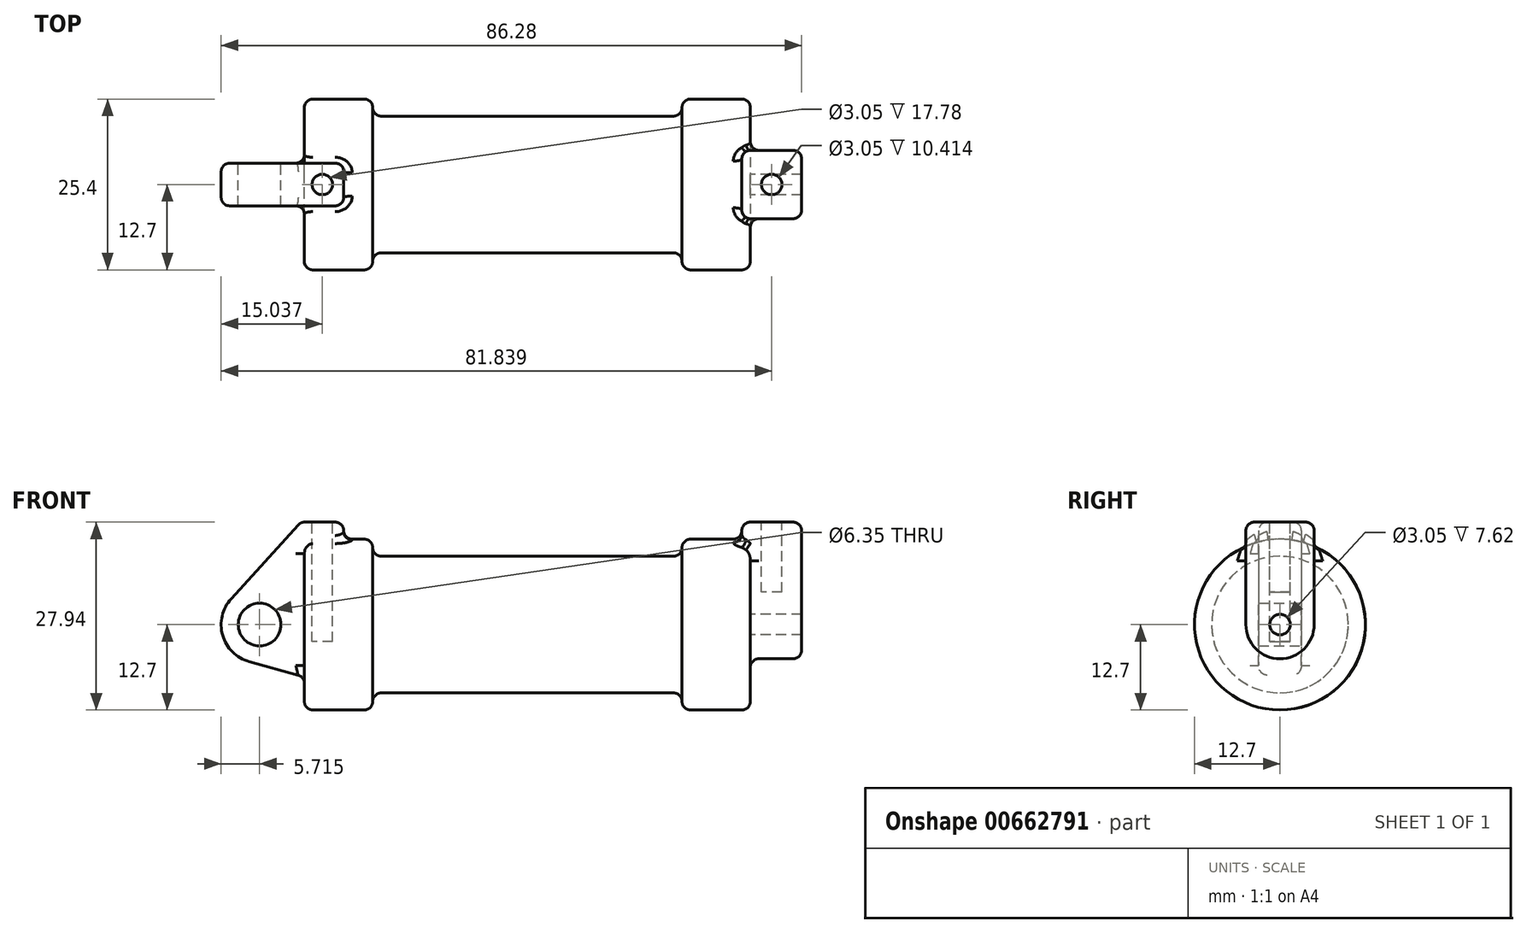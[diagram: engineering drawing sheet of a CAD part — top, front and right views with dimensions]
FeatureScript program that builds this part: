
annotation { "Feature Type Name" : "Feature", "Feature Type Description" : "" }
export const myFeature = defineFeature(function(context is Context, id is Id, definition is map)
    precondition{}
    {
        {
            var Q0;
            Q0=qCreatedBy(makeId("Front.planeOp"),FACE);
            var sketch = newSketch(context, id + "F0", { "sketchPlane" : qUnion([Q0])});
            skLineSegment(sketch, "E0", {"start": v(0, 0) * mm, "end": v(0, 12.7) * mm});
            skLineSegment(sketch, "E1", {"start": v(0, 12.7) * mm, "end": v(10.16, 12.7) * mm});
            skLineSegment(sketch, "E2", {"start": v(10.16, 12.7) * mm, "end": v(10.16, 10.16) * mm});
            skLineSegment(sketch, "E3", {"start": v(10.16, 10.16) * mm, "end": v(56.13, 10.16) * mm});
            skLineSegment(sketch, "E4", {"start": v(56.13, 10.16) * mm, "end": v(56.13, 12.7) * mm});
            skLineSegment(sketch, "E5", {"start": v(56.13, 12.7) * mm, "end": v(66.3, 12.7) * mm});
            skLineSegment(sketch, "E6", {"start": v(66.3, 12.7) * mm, "end": v(66.3, 0) * mm});
            skLineSegment(sketch, "E7", {"start": v(66.3, 0) * mm, "end": v(0, 0) * mm});
            skLineSegment(sketch, "E8", {"start": v(5.84, 15.24) * mm, "end": v(-0.5, 15.24) * mm});
            skLineSegment(sketch, "E9", {"start": v(-0.5, 15.24) * mm, "end": v(-10.88, 3.85) * mm});
            skLineSegment(sketch, "E10", {"start": v(0, 0) * mm, "end": v(-6.65, 0) * mm});
            skCircle(sketch, "E11", {"center": v(-6.65, 0) * mm, "radius": 5.72 * mm});
            skCircle(sketch, "E12", {"center": v(-6.65, 0) * mm, "radius": 3.18 * mm});
            skLineSegment(sketch, "E13", {"start": v(5.84, 15.24) * mm, "end": v(5.84, -9.4) * mm});
            skLineSegment(sketch, "E14", {"start": v(5.84, -9.4) * mm, "end": v(-8.18, -5.5) * mm});
            skSolve(sketch);
        }
        {
            var Q0;
            {var subQ0=sQuery(id+"F0.wireOp",EDGE,"E2");Q0=makeQuery(id+"F0.imprint","IMPRINT",FACE,{"disambiguationData":[TD([[makeQuery(id+"F0.imprint","IMPRINT",EDGE,{"derivedFrom":subQ0}),-1.0]])]});}
            var Q1;
            {var subQ0=sQuery(id+"F0.wireOp",EDGE,"E0");Q1=makeQuery(id+"F0.imprint","IMPRINT",FACE,{"disambiguationData":[TD([[makeQuery(id+"F0.imprint","IMPRINT",EDGE,{"derivedFrom":subQ0}),-1.0]])]});}
            var Q2;
            Q2=sQuery(id+"F0.wireOp",EDGE,"E7");
            revolve(context, id + "F1", {"entities" : qUnion([Q0, Q1]), "axis" : qUnion([Q2]), "revolveType" : RevolveType.FULL});
        }
        {
            var Q0;
            {var subQ1=sQuery(id+"F0.wireOp",EDGE,"E0");Q0=makeQuery(id+"F0.imprint","IMPRINT",FACE,{"disambiguationData":[TD([[makeQuery(id+"F0.imprint","IMPRINT",EDGE,{"derivedFrom":subQ1}),1.0]])]});}
            var Q1;
            {var subQ0=sQuery(id+"F0.wireOp",EDGE,"E0");Q1=makeQuery(id+"F0.imprint","IMPRINT",FACE,{"disambiguationData":[TD([[makeQuery(id+"F0.imprint","IMPRINT",EDGE,{"derivedFrom":subQ0}),-1.0]])]});}
            var Q2;
            {var subQ0=sQuery(id+"F0.wireOp",EDGE,"E14");Q2=makeQuery(id+"F0.imprint","IMPRINT",FACE,{"disambiguationData":[TD([[makeQuery(id+"F0.imprint","IMPRINT",EDGE,{"derivedFrom":subQ0}),-1.0]])]});}
            var Q3;
            {var subQ5=sQuery(id+"F0.wireOp",EDGE,"E12");Q3=makeQuery(id+"F0.imprint","IMPRINT",FACE,{"disambiguationData":[TD([[makeQuery(id+"F0.imprint","IMPRINT",EDGE,{"derivedFrom":subQ5}),-1.0]])]});}
            extrude(context, id + "F2", {"entities" : qUnion([Q0, Q1, Q2, Q3]), "operationType" : NewBodyOperationType.ADD, "endBound" : BoundingType.SYMMETRIC, "depth" : 6.35 * mm, "offsetDistance" : 25.4 * mm});
        }
        {
            var Q0;
            Q0=makeQuery(id+"F1.opRevolve","SWEPT_FACE",FACE,{"disambiguationData":[OSD([sQuery(id+"F0.wireOp",EDGE,"E6")])]});
            var sketch = newSketch(context, id + "F3", { "sketchPlane" : qUnion([Q0])});
            skCircle(sketch, "E15", {"center": v(0, 0) * mm, "radius": 1.52 * mm});
            skCircle(sketch, "E16", {"center": v(0, 0) * mm, "radius": 5.08 * mm});
            skLineSegment(sketch, "E17.bottom", {"start": v(-5.08, 15.24) * mm, "end": v(5.08, 15.24) * mm});
            skLineSegment(sketch, "E17.left", {"start": v(-5.08, 15.24) * mm, "end": v(-5.08, 0) * mm});
            skLineSegment(sketch, "E17.right", {"start": v(5.08, 15.24) * mm, "end": v(5.08, 0) * mm});
            skSolve(sketch);
        }
        {
            var Q0;
            Q0 = qSketchRegion(id + "F3", true);
            extrude(context, id + "F4", {"entities" : qUnion([Q0]), "operationType" : NewBodyOperationType.ADD, "depth" : 7.62 * mm, "offsetDistance" : 25.4 * mm, "hasSecondDirection" : true, "secondDirectionOppositeDirection" : true, "secondDirectionDepth" : 1.27 * mm});
        }
        {
            var Q0;
            Q0=makeQuery(id+"F4.opExtrude","SWEPT_FACE",FACE,{"disambiguationData":[OSD([sQuery(id+"F3.wireOp",EDGE,"E17.bottom")])]});
            var sketch = newSketch(context, id + "F5", { "sketchPlane" : qUnion([Q0])});
            skCircle(sketch, "E18", {"center": v(2.67, 0) * mm, "radius": 1.52 * mm});
            skCircle(sketch, "E19", {"center": v(69.47, 0) * mm, "radius": 1.52 * mm});
            skCircle(sketch, "E20", {"center": v(2.67, 0) * mm, "radius": 3.17 * mm, "construction": true});
            skLineSegment(sketch, "E21", {"start": v(73.91, 5.08) * mm, "end": v(65.02, -5.08) * mm, "construction": true});
            skLineSegment(sketch, "E22", {"start": v(65.02, 5.08) * mm, "end": v(73.91, -5.08) * mm, "construction": true});
            skSolve(sketch);
        }
        {
            var Q0;
            Q0=makeQuery(id+"F5.imprint","IMPRINT",FACE,{"disambiguationData":[TD([[makeQuery(id+"F5.imprint","IMPRINT",EDGE,{"derivedFrom":sQuery(id+"F5.wireOp",EDGE,"E18")}),1.0]])]});
            var Q1;
            Q1=sQuery(id+"F5.wireOp",EDGE,"E18");
            extrude(context, id + "F6", {"entities" : qUnion([Q0]), "operationType" : NewBodyOperationType.REMOVE, "surfaceEntities" : qUnion([Q1]), "oppositeDirection" : true, "depth" : 17.78 * mm, "offsetDistance" : 25.4 * mm});
        }
        {
            var Q0;
            Q0=makeQuery(id+"F4.opExtrude","SWEPT_FACE",FACE,{"disambiguationData":[OSD([sQuery(id+"F3.wireOp",EDGE,"E17.bottom")])]});
            var sketch = newSketch(context, id + "F7", { "sketchPlane" : qUnion([Q0])});
            skLineSegment(sketch, "E23.0", {"start": v(65.02, 5.08) * mm, "end": v(73.91, -5.08) * mm, "construction": true});
            skLineSegment(sketch, "E24.0", {"start": v(73.91, 5.08) * mm, "end": v(65.02, -5.08) * mm, "construction": true});
            skCircle(sketch, "E25.0", {"center": v(69.47, 0) * mm, "radius": 1.52 * mm});
            skSolve(sketch);
        }
        {
            var Q0;
            Q0=makeQuery(id+"F5.imprint","IMPRINT",FACE,{"disambiguationData":[TD([[makeQuery(id+"F5.imprint","IMPRINT",EDGE,{"derivedFrom":sQuery(id+"F5.wireOp",EDGE,"E19")}),1.0]])]});
            var Q1;
            Q1=sQuery(id+"F7.wireOp",EDGE,"E23.0");
            var Q2;
            Q2=sQuery(id+"F7.wireOp",EDGE,"E24.0");
            extrude(context, id + "F8", {"entities" : qUnion([Q0]), "operationType" : NewBodyOperationType.REMOVE, "surfaceEntities" : qUnion([Q1, Q2]), "oppositeDirection" : true, "depth" : 10.4 * mm, "offsetDistance" : 25.4 * mm});
        }
        {
            var Q0;
            Q0=makeQuery(id+"F1.opRevolve","SWEPT_EDGE",EDGE,{"disambiguationData":[OSD([sQuery(id+"F0.wireOp",EDGE,"E2"),sQuery(id+"F0.wireOp",EDGE,"E3")])]});
            var Q1;
            Q1=makeQuery(id+"F1.opRevolve","SWEPT_EDGE",EDGE,{"disambiguationData":[OSD([sQuery(id+"F0.wireOp",EDGE,"E1"),sQuery(id+"F0.wireOp",EDGE,"E2")])]});
            var Q2;
            Q2=makeQuery(id+"F1.opRevolve","SWEPT_EDGE",EDGE,{"disambiguationData":[OSD([sQuery(id+"F0.wireOp",EDGE,"E3"),sQuery(id+"F0.wireOp",EDGE,"E4")])]});
            var Q3;
            Q3=makeQuery(id+"F1.opRevolve","SWEPT_EDGE",EDGE,{"disambiguationData":[OSD([sQuery(id+"F0.wireOp",EDGE,"E4"),sQuery(id+"F0.wireOp",EDGE,"E5")])]});
            var Q4;
            Q4=makeQuery(id+"F1.opRevolve","SWEPT_EDGE",EDGE,{"disambiguationData":[OSD([sQuery(id+"F0.wireOp",EDGE,"E0"),sQuery(id+"F0.wireOp",EDGE,"E1")])]});
            var Q5;
            Q5=makeQuery(id+"F1.opRevolve","SWEPT_EDGE",EDGE,{"disambiguationData":[OSD([sQuery(id+"F0.wireOp",EDGE,"E5"),sQuery(id+"F0.wireOp",EDGE,"E6")])]});
            fillet(context, id + "F9", {"entities" : qUnion([Q0, Q1, Q2, Q3, Q4, Q5]), "radius" : 1.27 * mm, "tangentPropagation" : true, "allowEdgeOverflow" : false});
        }
        {
            var Q0;
            Q0=makeQuery(id+"F2.boolean.opBoolean","INTERSECT",EDGE,{"derivedFrom":[makeQuery(id+"F1.opRevolve","SWEPT_FACE",FACE,{"disambiguationData":[OSD([sQuery(id+"F0.wireOp",EDGE,"E0")])]}),makeQuery(id+"F2.opExtrude","CAP_FACE",FACE,{"disambiguationData":[OSD([sQuery(id+"F0.wireOp",EDGE,"E8"),sQuery(id+"F0.wireOp",EDGE,"E9"),sQuery(id+"F0.wireOp",EDGE,"E11"),sQuery(id+"F0.wireOp",EDGE,"E12"),sQuery(id+"F0.wireOp",EDGE,"E13"),sQuery(id+"F0.wireOp",EDGE,"E14")])],"isStart":false})]});
            var Q1;
            Q1=makeQuery(id+"F2.boolean.opBoolean","INTERSECT",EDGE,{"derivedFrom":[makeQuery(id+"F1.opRevolve","SWEPT_FACE",FACE,{"disambiguationData":[OSD([sQuery(id+"F0.wireOp",EDGE,"E1")])]}),makeQuery(id+"F2.opExtrude","CAP_FACE",FACE,{"disambiguationData":[OSD([sQuery(id+"F0.wireOp",EDGE,"E8"),sQuery(id+"F0.wireOp",EDGE,"E9"),sQuery(id+"F0.wireOp",EDGE,"E11"),sQuery(id+"F0.wireOp",EDGE,"E12"),sQuery(id+"F0.wireOp",EDGE,"E13"),sQuery(id+"F0.wireOp",EDGE,"E14")])],"isStart":false})]});
            var Q2;
            Q2=makeQuery(id+"F9.opFillet","BLEND_EDGE",EDGE,{"blendedFrom":[makeQuery(id+"F1.opRevolve","SWEPT_EDGE",EDGE,{"disambiguationData":[OSD([sQuery(id+"F0.wireOp",EDGE,"E0"),sQuery(id+"F0.wireOp",EDGE,"E1")])]}),makeQuery(id+"F2.opExtrude","CAP_FACE",FACE,{"disambiguationData":[OSD([sQuery(id+"F0.wireOp",EDGE,"E8"),sQuery(id+"F0.wireOp",EDGE,"E9"),sQuery(id+"F0.wireOp",EDGE,"E11"),sQuery(id+"F0.wireOp",EDGE,"E12"),sQuery(id+"F0.wireOp",EDGE,"E13"),sQuery(id+"F0.wireOp",EDGE,"E14")])],"isStart":false})],"blendedInto":[makeQuery(id+"F2.opExtrude","CAP_FACE",FACE,{"disambiguationData":[OSD([sQuery(id+"F0.wireOp",EDGE,"E8"),sQuery(id+"F0.wireOp",EDGE,"E9"),sQuery(id+"F0.wireOp",EDGE,"E11"),sQuery(id+"F0.wireOp",EDGE,"E12"),sQuery(id+"F0.wireOp",EDGE,"E13"),sQuery(id+"F0.wireOp",EDGE,"E14")])],"isStart":false})]});
            var Q3;
            Q3=makeQuery(id+"F2.opExtrude","CAP_EDGE",EDGE,{"disambiguationData":[OSD([sQuery(id+"F0.wireOp",EDGE,"E13")])],"isStart":false});
            var Q4;
            Q4=makeQuery(id+"F2.opExtrude","CAP_EDGE",EDGE,{"disambiguationData":[OSD([sQuery(id+"F0.wireOp",EDGE,"E8")])],"isStart":false});
            var Q5;
            Q5=makeQuery(id+"F2.opExtrude","CAP_EDGE",EDGE,{"disambiguationData":[OSD([sQuery(id+"F0.wireOp",EDGE,"E9")])],"isStart":false});
            var Q6;
            Q6=makeQuery(id+"F2.opExtrude","CAP_EDGE",EDGE,{"disambiguationData":[OSD([sQuery(id+"F0.wireOp",EDGE,"E11")])],"isStart":false});
            var Q7;
            Q7=makeQuery(id+"F2.opExtrude","CAP_EDGE",EDGE,{"disambiguationData":[OSD([sQuery(id+"F0.wireOp",EDGE,"E14")])],"isStart":false});
            var Q8;
            Q8=makeQuery(id+"F2.opExtrude","CAP_EDGE",EDGE,{"disambiguationData":[OSD([sQuery(id+"F0.wireOp",EDGE,"E13")])],"isStart":true});
            var Q9;
            Q9=makeQuery(id+"F2.opExtrude","CAP_EDGE",EDGE,{"disambiguationData":[OSD([sQuery(id+"F0.wireOp",EDGE,"E8")])],"isStart":true});
            var Q10;
            Q10=makeQuery(id+"F2.opExtrude","CAP_EDGE",EDGE,{"disambiguationData":[OSD([sQuery(id+"F0.wireOp",EDGE,"E9")])],"isStart":true});
            var Q11;
            Q11=makeQuery(id+"F2.opExtrude","CAP_EDGE",EDGE,{"disambiguationData":[OSD([sQuery(id+"F0.wireOp",EDGE,"E11")])],"isStart":true});
            var Q12;
            Q12=makeQuery(id+"F2.opExtrude","CAP_EDGE",EDGE,{"disambiguationData":[OSD([sQuery(id+"F0.wireOp",EDGE,"E14")])],"isStart":true});
            var Q13;
            Q13=makeQuery(id+"F2.boolean.opBoolean","INTERSECT",EDGE,{"derivedFrom":[makeQuery(id+"F1.opRevolve","SWEPT_FACE",FACE,{"disambiguationData":[OSD([sQuery(id+"F0.wireOp",EDGE,"E0")])]}),makeQuery(id+"F2.opExtrude","CAP_FACE",FACE,{"disambiguationData":[OSD([sQuery(id+"F0.wireOp",EDGE,"E8"),sQuery(id+"F0.wireOp",EDGE,"E9"),sQuery(id+"F0.wireOp",EDGE,"E11"),sQuery(id+"F0.wireOp",EDGE,"E12"),sQuery(id+"F0.wireOp",EDGE,"E13"),sQuery(id+"F0.wireOp",EDGE,"E14")])],"isStart":true})]});
            var Q14;
            Q14=makeQuery(id+"F2.boolean.opBoolean","INTERSECT",EDGE,{"derivedFrom":[makeQuery(id+"F1.opRevolve","SWEPT_FACE",FACE,{"disambiguationData":[OSD([sQuery(id+"F0.wireOp",EDGE,"E1")])]}),makeQuery(id+"F2.opExtrude","CAP_FACE",FACE,{"disambiguationData":[OSD([sQuery(id+"F0.wireOp",EDGE,"E8"),sQuery(id+"F0.wireOp",EDGE,"E9"),sQuery(id+"F0.wireOp",EDGE,"E11"),sQuery(id+"F0.wireOp",EDGE,"E12"),sQuery(id+"F0.wireOp",EDGE,"E13"),sQuery(id+"F0.wireOp",EDGE,"E14")])],"isStart":true})]});
            var Q15;
            Q15=makeQuery(id+"F9.opFillet","BLEND_EDGE",EDGE,{"blendedFrom":[makeQuery(id+"F1.opRevolve","SWEPT_EDGE",EDGE,{"disambiguationData":[OSD([sQuery(id+"F0.wireOp",EDGE,"E0"),sQuery(id+"F0.wireOp",EDGE,"E1")])]}),makeQuery(id+"F2.opExtrude","CAP_FACE",FACE,{"disambiguationData":[OSD([sQuery(id+"F0.wireOp",EDGE,"E8"),sQuery(id+"F0.wireOp",EDGE,"E9"),sQuery(id+"F0.wireOp",EDGE,"E11"),sQuery(id+"F0.wireOp",EDGE,"E12"),sQuery(id+"F0.wireOp",EDGE,"E13"),sQuery(id+"F0.wireOp",EDGE,"E14")])],"isStart":true})],"blendedInto":[makeQuery(id+"F2.opExtrude","CAP_FACE",FACE,{"disambiguationData":[OSD([sQuery(id+"F0.wireOp",EDGE,"E8"),sQuery(id+"F0.wireOp",EDGE,"E9"),sQuery(id+"F0.wireOp",EDGE,"E11"),sQuery(id+"F0.wireOp",EDGE,"E12"),sQuery(id+"F0.wireOp",EDGE,"E13"),sQuery(id+"F0.wireOp",EDGE,"E14")])],"isStart":true})]});
            var Q16;
            Q16=makeQuery(id+"F2.opExtrude","SWEPT_EDGE",EDGE,{"disambiguationData":[OSD([sQuery(id+"F0.wireOp",EDGE,"E8"),sQuery(id+"F0.wireOp",EDGE,"E9")])]});
            var Q17;
            Q17=makeQuery(id+"F2.opExtrude","SWEPT_EDGE",EDGE,{"disambiguationData":[OSD([sQuery(id+"F0.wireOp",EDGE,"E8"),sQuery(id+"F0.wireOp",EDGE,"E13")])]});
            var Q18;
            Q18=makeQuery(id+"F2.boolean.opBoolean","INTERSECT",EDGE,{"derivedFrom":[makeQuery(id+"F1.opRevolve","SWEPT_FACE",FACE,{"disambiguationData":[OSD([sQuery(id+"F0.wireOp",EDGE,"E1")])]}),makeQuery(id+"F2.opExtrude","SWEPT_FACE",FACE,{"disambiguationData":[OSD([sQuery(id+"F0.wireOp",EDGE,"E13")])]})]});
            var Q19;
            Q19=makeQuery(id+"F2.boolean.opBoolean","INTERSECT",EDGE,{"derivedFrom":[makeQuery(id+"F1.opRevolve","SWEPT_FACE",FACE,{"disambiguationData":[OSD([sQuery(id+"F0.wireOp",EDGE,"E0")])]}),makeQuery(id+"F2.opExtrude","SWEPT_FACE",FACE,{"disambiguationData":[OSD([sQuery(id+"F0.wireOp",EDGE,"E14")])]})]});
            fillet(context, id + "F10", {"entities" : qUnion([Q0, Q1, Q2, Q3, Q4, Q5, Q6, Q7, Q8, Q9, Q10, Q11, Q12, Q13, Q14, Q15, Q16, Q17, Q18, Q19]), "radius" : 1.27 * mm, "tangentPropagation" : true, "allowEdgeOverflow" : false});
        }
        {
            var Q0;
            Q0=makeQuery(id+"F4.opExtrude","CAP_EDGE",EDGE,{"disambiguationData":[OSD([sQuery(id+"F3.wireOp",EDGE,"E17.bottom")])],"isStart":false});
            var Q1;
            Q1=makeQuery(id+"F4.opExtrude","SWEPT_EDGE",EDGE,{"disambiguationData":[OSD([sQuery(id+"F3.wireOp",EDGE,"E17.bottom"),sQuery(id+"F3.wireOp",EDGE,"E17.left")])]});
            var Q2;
            Q2=makeQuery(id+"F4.opExtrude","CAP_EDGE",EDGE,{"disambiguationData":[OSD([sQuery(id+"F3.wireOp",EDGE,"E17.bottom")])],"isStart":true});
            var Q3;
            Q3=makeQuery(id+"F4.opExtrude","SWEPT_EDGE",EDGE,{"disambiguationData":[OSD([sQuery(id+"F3.wireOp",EDGE,"E17.bottom"),sQuery(id+"F3.wireOp",EDGE,"E17.right")])]});
            var Q4;
            Q4=makeQuery(id+"F4.opExtrude","CAP_EDGE",EDGE,{"disambiguationData":[OSD([sQuery(id+"F3.wireOp",EDGE,"E17.right")])],"isStart":false});
            var Q5;
            Q5=makeQuery(id+"F4.opExtrude","CAP_EDGE",EDGE,{"disambiguationData":[OSD([sQuery(id+"F3.wireOp",EDGE,"E17.left")])],"isStart":false});
            var Q6;
            Q6=makeQuery(id+"F4.opExtrude","CAP_EDGE",EDGE,{"disambiguationData":[OSD([sQuery(id+"F3.wireOp",EDGE,"E16")])],"isStart":false});
            var Q7;
            Q7=makeQuery(id+"F4.boolean.opBoolean","INTERSECT",EDGE,{"derivedFrom":[makeQuery(id+"F1.opRevolve","SWEPT_FACE",FACE,{"disambiguationData":[OSD([sQuery(id+"F0.wireOp",EDGE,"E6")])]}),makeQuery(id+"F4.opExtrude","SWEPT_FACE",FACE,{"disambiguationData":[OSD([sQuery(id+"F3.wireOp",EDGE,"E17.left")])]})]});
            var Q8;
            Q8=makeQuery(id+"F4.opExtrude","CAP_EDGE",EDGE,{"disambiguationData":[OSD([sQuery(id+"F3.wireOp",EDGE,"E17.left")])],"isStart":true});
            var Q9;
            Q9=makeQuery(id+"F9.opFillet","BLEND_EDGE",EDGE,{"blendedFrom":[makeQuery(id+"F1.opRevolve","SWEPT_EDGE",EDGE,{"disambiguationData":[OSD([sQuery(id+"F0.wireOp",EDGE,"E5"),sQuery(id+"F0.wireOp",EDGE,"E6")])]}),makeQuery(id+"F4.opExtrude","SWEPT_FACE",FACE,{"disambiguationData":[OSD([sQuery(id+"F3.wireOp",EDGE,"E17.left")])]})],"blendedInto":[makeQuery(id+"F4.opExtrude","SWEPT_FACE",FACE,{"disambiguationData":[OSD([sQuery(id+"F3.wireOp",EDGE,"E17.left")])]})]});
            var Q10;
            Q10=makeQuery(id+"F4.boolean.opBoolean","INTERSECT",EDGE,{"derivedFrom":[makeQuery(id+"F1.opRevolve","SWEPT_FACE",FACE,{"disambiguationData":[OSD([sQuery(id+"F0.wireOp",EDGE,"E6")])]}),makeQuery(id+"F4.opExtrude","SWEPT_FACE",FACE,{"disambiguationData":[OSD([sQuery(id+"F3.wireOp",EDGE,"E16")])]})]});
            var Q11;
            Q11=makeQuery(id+"F4.boolean.opBoolean","INTERSECT",EDGE,{"derivedFrom":[makeQuery(id+"F1.opRevolve","SWEPT_FACE",FACE,{"disambiguationData":[OSD([sQuery(id+"F0.wireOp",EDGE,"E6")])]}),makeQuery(id+"F4.opExtrude","SWEPT_FACE",FACE,{"disambiguationData":[OSD([sQuery(id+"F3.wireOp",EDGE,"E17.right")])]})]});
            var Q12;
            Q12=makeQuery(id+"F9.opFillet","BLEND_EDGE",EDGE,{"blendedFrom":[makeQuery(id+"F1.opRevolve","SWEPT_EDGE",EDGE,{"disambiguationData":[OSD([sQuery(id+"F0.wireOp",EDGE,"E5"),sQuery(id+"F0.wireOp",EDGE,"E6")])]}),makeQuery(id+"F4.opExtrude","SWEPT_FACE",FACE,{"disambiguationData":[OSD([sQuery(id+"F3.wireOp",EDGE,"E17.right")])]})],"blendedInto":[makeQuery(id+"F4.opExtrude","SWEPT_FACE",FACE,{"disambiguationData":[OSD([sQuery(id+"F3.wireOp",EDGE,"E17.right")])]})]});
            var Q13;
            Q13=makeQuery(id+"F4.opExtrude","CAP_EDGE",EDGE,{"disambiguationData":[OSD([sQuery(id+"F3.wireOp",EDGE,"E17.right")])],"isStart":true});
            var Q14;
            Q14=makeQuery(id+"F4.boolean.opBoolean","INTERSECT",EDGE,{"derivedFrom":[makeQuery(id+"F1.opRevolve","SWEPT_FACE",FACE,{"disambiguationData":[OSD([sQuery(id+"F0.wireOp",EDGE,"E5")])]}),makeQuery(id+"F4.opExtrude","CAP_FACE",FACE,{"disambiguationData":[OSD([sQuery(id+"F3.wireOp",EDGE,"E15"),sQuery(id+"F3.wireOp",EDGE,"E16"),sQuery(id+"F3.wireOp",EDGE,"E17.bottom"),sQuery(id+"F3.wireOp",EDGE,"E17.left"),sQuery(id+"F3.wireOp",EDGE,"E17.right")])],"isStart":true})]});
            fillet(context, id + "F11", {"entities" : qUnion([Q0, Q1, Q2, Q3, Q4, Q5, Q6, Q7, Q8, Q9, Q10, Q11, Q12, Q13, Q14]), "radius" : 1.27 * mm, "tangentPropagation" : true, "allowEdgeOverflow" : false});
        }
    });
